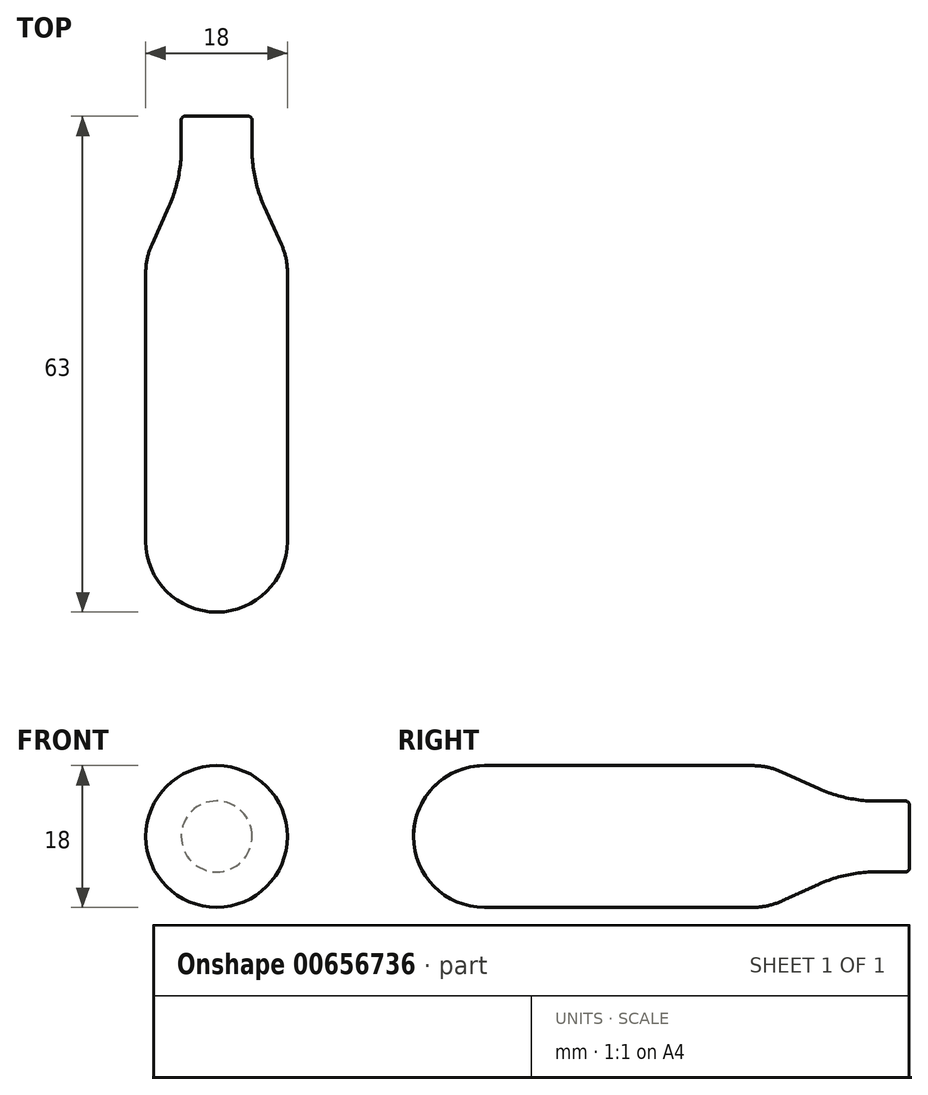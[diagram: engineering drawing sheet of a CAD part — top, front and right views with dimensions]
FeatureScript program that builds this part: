
annotation { "Feature Type Name" : "Feature", "Feature Type Description" : "" }
export const myFeature = defineFeature(function(context is Context, id is Id, definition is map)
    precondition{}
    {
        {
            var Q0;
            Q0=qCreatedBy(makeId("Right.planeOp"),FACE);
            var sketch = newSketch(context, id + "F0", { "sketchPlane" : qUnion([Q0])});
            skLineSegment(sketch, "E0", {"start": v(0, 0) * mm, "end": v(0, 4.5) * mm});
            skLineSegment(sketch, "E1", {"start": v(0, 4.5) * mm, "end": v(-8, 4.5) * mm});
            skLineSegment(sketch, "E2", {"start": v(-8, 4.5) * mm, "end": v(-18, 9) * mm});
            skLineSegment(sketch, "E3", {"start": v(-18, 9) * mm, "end": v(-63, 9) * mm});
            skLineSegment(sketch, "E4", {"start": v(-63, 9) * mm, "end": v(-63, 0) * mm});
            skLineSegment(sketch, "E5", {"start": v(-63, 0) * mm, "end": v(0, 0) * mm});
            skSolve(sketch);
        }
        {
            var Q0;
            Q0=makeQuery(id+"F0.imprint","IMPRINT",FACE,{"disambiguationData":[TD([[makeQuery(id+"F0.imprint","IMPRINT",EDGE,{"derivedFrom":sQuery(id+"F0.wireOp",EDGE,"E0")}),1.0]])]});
            var Q1;
            Q1=sQuery(id+"F0.wireOp",EDGE,"E5");
            revolve(context, id + "F1", {"entities" : qUnion([Q0]), "axis" : qUnion([Q1]), "revolveType" : RevolveType.FULL, "surfaceOperationType" : NewSurfaceOperationType.NEW});
        }
        {
            var Q0;
            Q0=makeQuery(id+"F1.opRevolve","SWEPT_EDGE",EDGE,{"disambiguationData":[OSD([sQuery(id+"F0.wireOp",EDGE,"E3"),sQuery(id+"F0.wireOp",EDGE,"E4")])]});
            fillet(context, id + "F2", {"entities" : qUnion([Q0]), "radius" : 9 * mm, "tangentPropagation" : true, "defaultsChanged" : false, "vertexSettings" : [], "allowEdgeOverflow" : false});
        }
        {
            var Q0;
            Q0=makeQuery(id+"F1.opRevolve","SWEPT_EDGE",EDGE,{"disambiguationData":[OSD([sQuery(id+"F0.wireOp",EDGE,"E2"),sQuery(id+"F0.wireOp",EDGE,"E3")])]});
            fillet(context, id + "F3", {"entities" : qUnion([Q0]), "radius" : 8.78 * mm, "tangentPropagation" : true, "defaultsChanged" : false, "vertexSettings" : [], "allowEdgeOverflow" : false});
        }
        {
            var Q0;
            Q0=makeQuery(id+"F1.opRevolve","SWEPT_FACE",FACE,{"disambiguationData":[OSD([sQuery(id+"F0.wireOp",EDGE,"E2")])]});
            fillet(context, id + "F4", {"entities" : qUnion([Q0]), "radius" : 17.56 * mm, "tangentPropagation" : true, "defaultsChanged" : false, "vertexSettings" : [], "allowEdgeOverflow" : false});
        }
        {
            var Q0;
            Q0=makeQuery(id+"F1.opRevolve","SWEPT_EDGE",EDGE,{"disambiguationData":[OSD([sQuery(id+"F0.wireOp",EDGE,"E0"),sQuery(id+"F0.wireOp",EDGE,"E1")])]});
            fillet(context, id + "F5", {"entities" : qUnion([Q0]), "radius" : .5 * mm, "tangentPropagation" : true, "defaultsChanged" : false, "vertexSettings" : [], "allowEdgeOverflow" : false});
        }
    });
